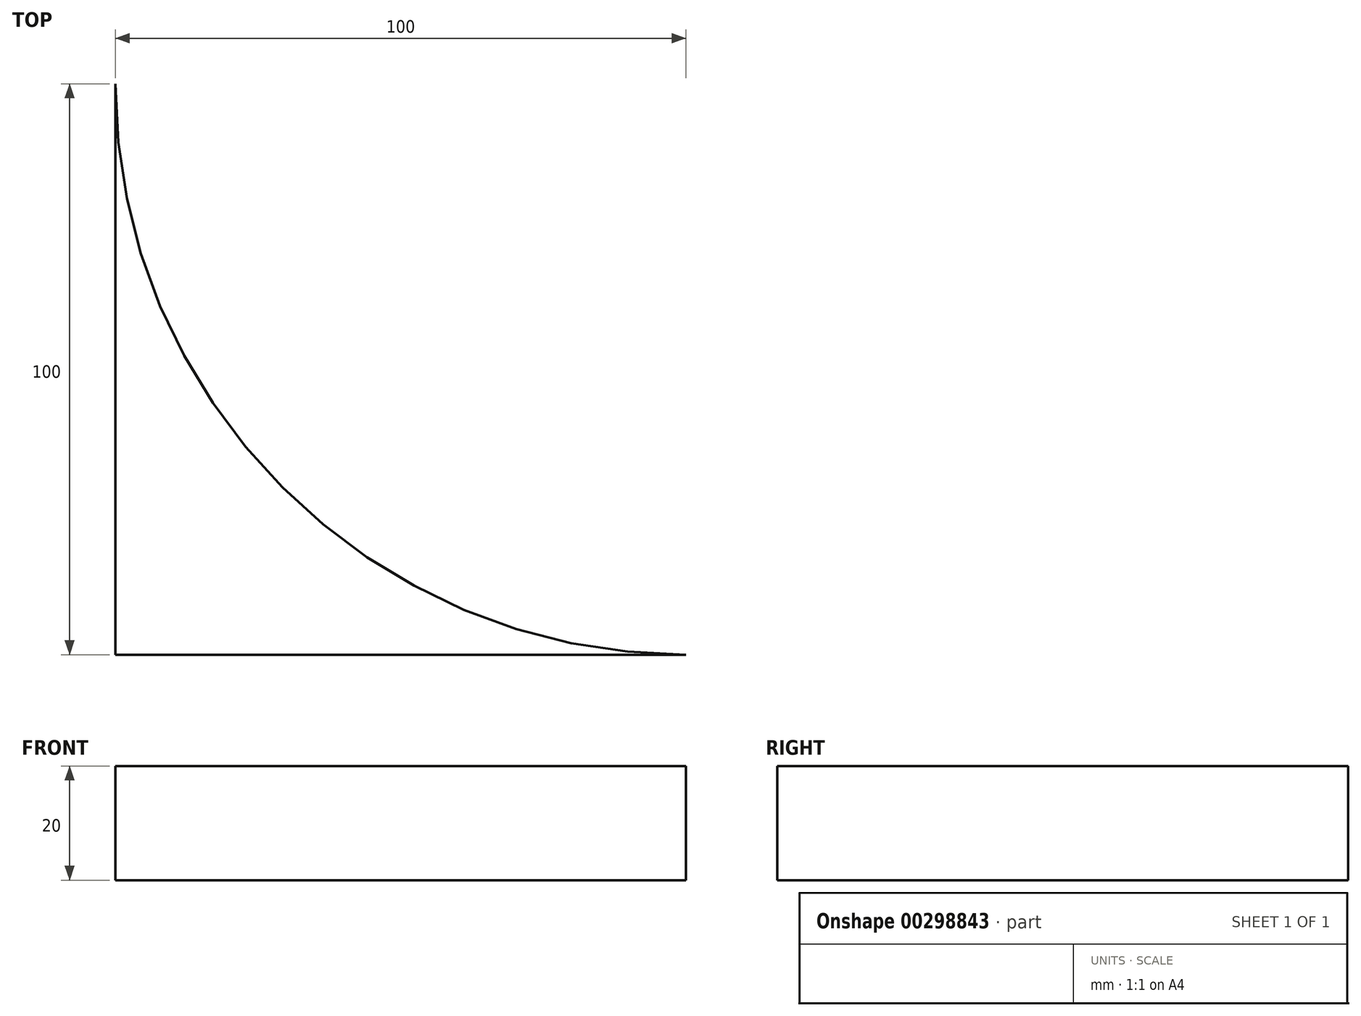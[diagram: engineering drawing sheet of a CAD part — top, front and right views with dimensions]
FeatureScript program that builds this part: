
annotation { "Feature Type Name" : "Feature", "Feature Type Description" : "" }
export const myFeature = defineFeature(function(context is Context, id is Id, definition is map)
    precondition{}
    {
        {
            var Q0;
            Q0=qCreatedBy(makeId("Top.planeOp"),FACE);
            var sketch = newSketch(context, id + "F0", { "sketchPlane" : qUnion([Q0])});
            skLineSegment(sketch, "E0", {"start": v(0, 0) * mm, "end": v(0, 100) * mm});
            skLineSegment(sketch, "E1", {"start": v(0, 0) * mm, "end": v(100, 0) * mm});
            skArc(sketch, "E2", {"start": v(0, 100) * mm, "mid": v(29.29, 29.29) * mm, "end": v(100, 0) * mm});
            skSolve(sketch);
        }
        {
            var Q0;
            Q0=makeQuery(id+"F0.imprint","IMPRINT",FACE,{"disambiguationData":[TD([[makeQuery(id+"F0.imprint","IMPRINT",EDGE,{"derivedFrom":sQuery(id+"F0.wireOp",EDGE,"E0")}),-1.0]])]});
            extrude(context, id + "F1", {"entities" : qUnion([Q0]), "endBound" : BoundingType.SYMMETRIC, "depth" : 20 * mm});
        }
    });
